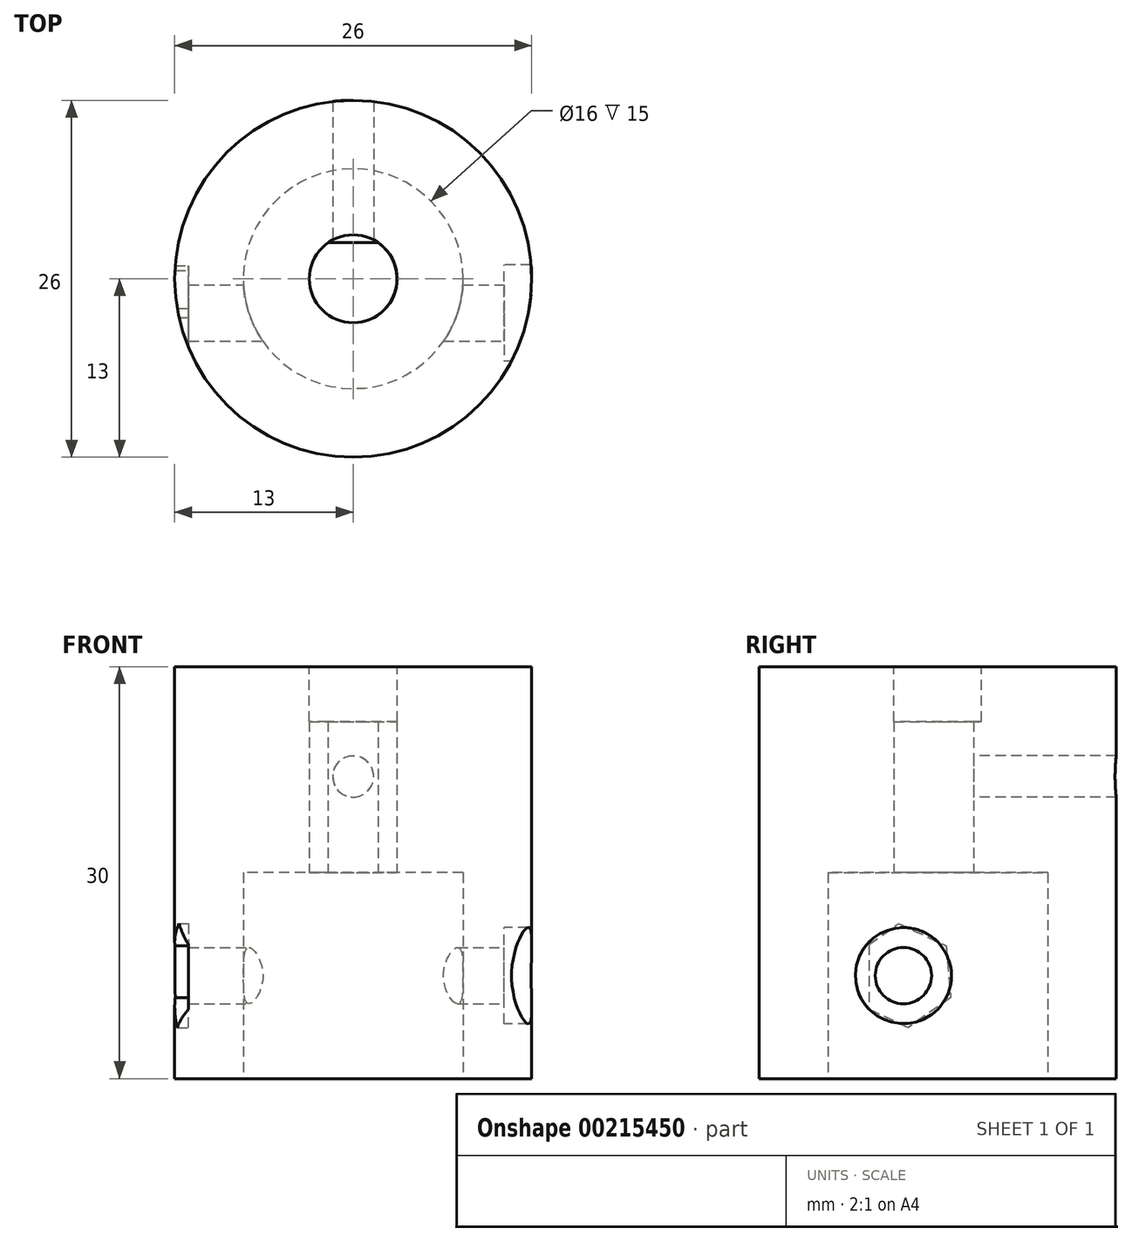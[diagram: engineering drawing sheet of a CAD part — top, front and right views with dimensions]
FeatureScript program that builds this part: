
annotation { "Feature Type Name" : "Feature", "Feature Type Description" : "" }
export const myFeature = defineFeature(function(context is Context, id is Id, definition is map)
    precondition{}
    {
        {
            var Q0;
            Q0=qCreatedBy(makeId("Top.planeOp"),FACE);
            var sketch = newSketch(context, id + "F0", { "sketchPlane" : qUnion([Q0])});
            skCircle(sketch, "E0", {"center": v(0, 0) * mm, "radius": 13 * mm});
            skSolve(sketch);
        }
        {
            var Q0;
            Q0=qCreatedBy(makeId("Top.planeOp"),FACE);
            cPlane(context, id + "F1", {"entities" : qUnion([Q0]), "cplaneType" : CPlaneType.OFFSET, "offset" : 15 * mm, "width" : 150 * mm, "height" : 150 * mm});
        }
        {
            var Q0;
            Q0=qCreatedBy(makeId("Top.planeOp"),FACE);
            cPlane(context, id + "F2", {"entities" : qUnion([Q0]), "cplaneType" : CPlaneType.OFFSET, "offset" : 15 * mm, "oppositeDirection" : true, "width" : 150 * mm, "height" : 150 * mm});
        }
        {
            var Q0;
            Q0=qCreatedBy(id+"F1.planeOp",FACE);
            var sketch = newSketch(context, id + "F3", { "sketchPlane" : qUnion([Q0])});
            skCircle(sketch, "E1", {"center": v(0, 0) * mm, "radius": 3.2 * mm});
            skSolve(sketch);
        }
        {
            var Q0;
            Q0=qCreatedBy(id+"F2.planeOp",FACE);
            var sketch = newSketch(context, id + "F4", { "sketchPlane" : qUnion([Q0])});
            skCircle(sketch, "E2", {"center": v(0, 0) * mm, "radius": 8 * mm});
            skSolve(sketch);
        }
        {
            var Q0;
            Q0=qSketchRegion(id+"F0",true);
            extrude(context, id + "F5", {"entities" : qUnion([Q0]), "depth" : 30 * mm, "symmetric" : true});
        }
        {
            var Q0;
            Q0=qSketchRegion(id+"F4",true);
            extrude(context, id + "F6", {"entities" : qUnion([Q0]), "operationType" : NewBodyOperationType.REMOVE, "depth" : 15 * mm});
        }
        {
            var Q0;
            Q0=qCreatedBy(makeId("Top.planeOp"),FACE);
            var sketch = newSketch(context, id + "F7", { "sketchPlane" : qUnion([Q0])});
            skLineSegment(sketch, "E3", {"start": v(-1.84, 2.62) * mm, "end": v(1.82, 2.62) * mm});
            skArc(sketch, "E4", {"start": v(-1.84, 2.62) * mm, "mid": v(-0.01, -3.2) * mm, "end": v(1.82, 2.62) * mm});
            skSolve(sketch);
        }
        {
            var Q0;
            Q0=qSketchRegion(id+"F3",true);
            extrude(context, id + "F8", {"entities" : qUnion([Q0]), "operationType" : NewBodyOperationType.REMOVE, "oppositeDirection" : true, "depth" : 4 * mm});
        }
        {
            var Q0;
            Q0=qSketchRegion(id+"F7",true);
            extrude(context, id + "F9", {"entities" : qUnion([Q0]), "operationType" : NewBodyOperationType.REMOVE, "depth" : 11 * mm});
        }
        {
            var Q0;
            Q0=qCreatedBy(makeId("Right.planeOp"),FACE);
            var sketch = newSketch(context, id + "F10", { "sketchPlane" : qUnion([Q0])});
            skCircle(sketch, "E5", {"center": v(-2.5, -7.5) * mm, "radius": 2.05 * mm});
            skSolve(sketch);
        }
        {
            var Q0;
            Q0 = qSketchRegion(id + "F10", true);
            extrude(context, id + "F11", {"entities" : qUnion([Q0]), "operationType" : NewBodyOperationType.REMOVE, "oppositeDirection" : true, "depth" : 30 * mm, "symmetric" : true});
        }
        {
            var Q0;
            Q0=qCreatedBy(makeId("Front.planeOp"),FACE);
            var sketch = newSketch(context, id + "F12", { "sketchPlane" : qUnion([Q0])});
            skCircle(sketch, "E6", {"center": v(0, 7) * mm, "radius": 1.5 * mm});
            skSolve(sketch);
        }
        {
            var Q0;
            Q0 = qSketchRegion(id + "F12", true);
            extrude(context, id + "F13", {"entities" : qUnion([Q0]), "operationType" : NewBodyOperationType.REMOVE, "oppositeDirection" : true, "depth" : 25 * mm});
        }
        {
            var Q0;
            Q0=qCreatedBy(makeId("Right.planeOp"),FACE);
            cPlane(context, id + "F14", {"entities" : qUnion([Q0]), "cplaneType" : CPlaneType.OFFSET, "offset" : 11 * mm, "width" : 150 * mm, "height" : 150 * mm});
        }
        {
            var Q0;
            Q0=qCreatedBy(id+"F14.planeOp",FACE);
            var sketch = newSketch(context, id + "F15", { "sketchPlane" : qUnion([Q0])});
            skCircle(sketch, "E7", {"center": v(-2.5, -7.5) * mm, "radius": 3.5 * mm});
            skSolve(sketch);
        }
        {
            var Q0;
            Q0 = qSketchRegion(id + "F15", true);
            extrude(context, id + "F16", {"entities" : qUnion([Q0]), "operationType" : NewBodyOperationType.REMOVE, "depth" : 5 * mm});
        }
        {
            var Q0;
            Q0=qCreatedBy(makeId("Right.planeOp"),FACE);
            cPlane(context, id + "F17", {"entities" : qUnion([Q0]), "cplaneType" : CPlaneType.OFFSET, "offset" : 12 * mm, "oppositeDirection" : true, "width" : 150 * mm, "height" : 150 * mm});
        }
        {
            var Q0;
            Q0=qCreatedBy(id+"F17.planeOp",FACE);
            var sketch = newSketch(context, id + "F18", { "sketchPlane" : qUnion([Q0])});
            skCircle(sketch, "E8.cCircle", {"center": v(-2.5, -7.5) * mm, "radius": 3.8 * mm, "construction": true});
            skLineSegment(sketch, "E8.0", {"start": v(-5.6, -9.68) * mm, "end": v(-5.95, -5.9) * mm});
            skLineSegment(sketch, "E8.1", {"start": v(-5.95, -5.9) * mm, "end": v(-2.84, -3.71) * mm});
            skLineSegment(sketch, "E8.2", {"start": v(-2.84, -3.71) * mm, "end": v(0.6, -5.32) * mm});
            skLineSegment(sketch, "E8.3", {"start": v(0.6, -5.32) * mm, "end": v(0.95, -9.1) * mm});
            skLineSegment(sketch, "E8.4", {"start": v(0.95, -9.1) * mm, "end": v(-2.16, -11.29) * mm});
            skLineSegment(sketch, "E8.5", {"start": v(-2.16, -11.29) * mm, "end": v(-5.6, -9.68) * mm});
            skSolve(sketch);
        }
        {
            var Q0;
            Q0 = qSketchRegion(id + "F18", true);
            extrude(context, id + "F19", {"entities" : qUnion([Q0]), "operationType" : NewBodyOperationType.REMOVE, "oppositeDirection" : true, "depth" : 3 * mm});
        }
    });
